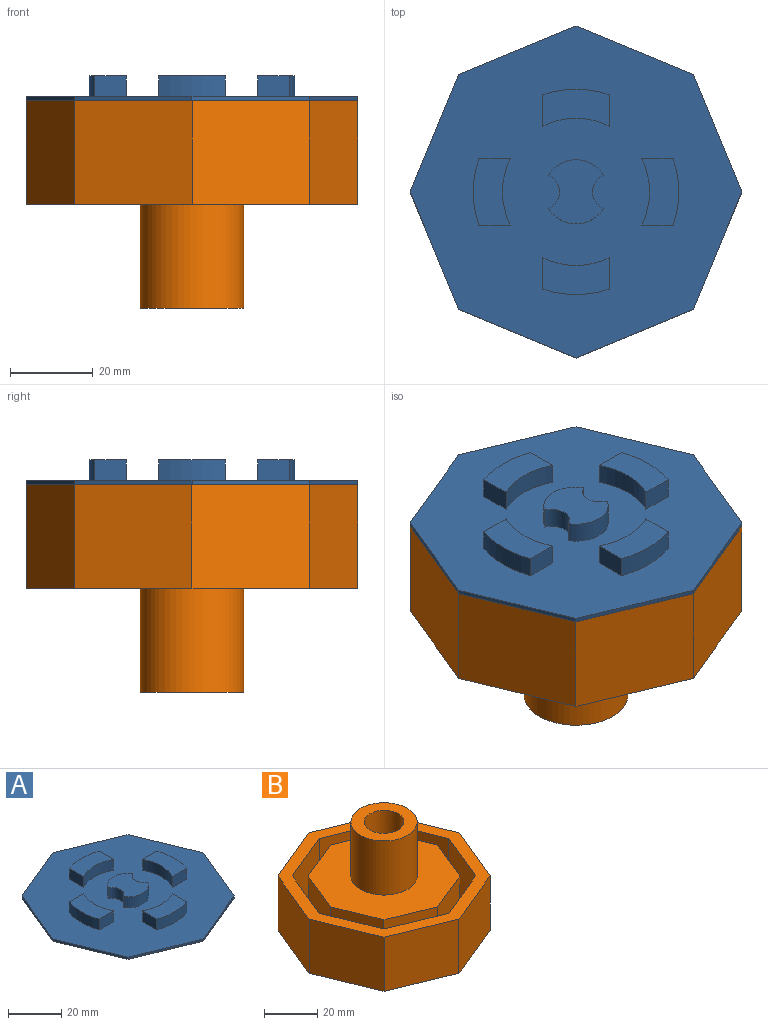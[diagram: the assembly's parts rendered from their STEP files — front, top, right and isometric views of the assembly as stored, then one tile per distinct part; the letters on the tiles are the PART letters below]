
ASSEMBLY  parts=2 mates=1
PART A: 35 faces, bbox 80x80x6 mm
  f0: plane 80x80mm, normal (0,0,1), area 3919.6mm2, adj f1,f2,f3,f4,f5,f6,f7,f8
  f1: plane 28.28x11.72mm, normal (-0.38,-0.92,0), area 30.6mm2, adj f0,f2,f8,f9
  f2: plane 28.28x11.72mm, normal (0.38,-0.92,0), area 30.6mm2, adj f0,f1,f3,f9
  f3: plane 28.28x11.72mm, normal (0.92,-0.38,0), area 30.6mm2, adj f0,f2,f4,f9
  f4: plane 28.28x11.72mm, normal (0.92,0.38,0), area 30.6mm2, adj f0,f3,f5,f9
  f5: plane 28.28x11.72mm, normal (0.38,0.92,0), area 30.6mm2, adj f0,f4,f6,f9
  f6: plane 28.28x11.72mm, normal (-0.38,0.92,0), area 30.6mm2, adj f0,f5,f7,f9
  f7: plane 28.28x11.72mm, normal (-0.92,0.38,0), area 30.6mm2, adj f0,f6,f8,f9
  f8: plane 28.28x11.72mm, normal (-0.92,-0.38,0), area 30.6mm2, adj f0,f1,f7,f9
  f9: plane 80x80mm, normal (0,0,-1), area 4525.5mm2, adj f1,f2,f3,f4,f5,f6,f7,f8
  f10: plane 7.58x5mm, normal (1,0,0), area 37.9mm2, adj f0,f11,f13,f14
  f11: cylinder r=24.75mm len=16mm, axis (0,0,-1), area 81.5mm2, adj f0,f10,f12,f14
  f12: plane 7.58x5mm, normal (-1,0,0), area 37.9mm2, adj f0,f11,f13,f14
  f13: cylinder r=17.75mm len=16mm, axis (0,0,-1), area 83mm2, adj f0,f10,f12,f14
  f14: plane 16x8.91mm, normal (0,0,1), area 114.9mm2, adj f10,f11,f12,f13
  f15: plane 16x8.91mm, normal (0,0,1), area 114.9mm2, adj f16,f17,f18,f19
  f16: cylinder r=17.75mm len=16mm, axis (0,0,-1), area 83mm2, adj f0,f15,f17,f19
  f17: plane 7.58x5mm, normal (1,0,0), area 37.9mm2, adj f0,f15,f16,f18
  f18: cylinder r=24.75mm len=16mm, axis (0,0,-1), area 81.5mm2, adj f0,f15,f17,f19
  f19: plane 7.58x5mm, normal (-1,0,0), area 37.9mm2, adj f0,f15,f16,f18
  f20: plane 16x8.91mm, normal (0,0,1), area 114.9mm2, adj f21,f22,f23,f24
  f21: plane 7.58x5mm, normal (0,-1,0), area 37.9mm2, adj f0,f20,f22,f24
  f22: cylinder r=24.75mm len=16mm, axis (0,0,-1), area 81.5mm2, adj f0,f20,f21,f23
  f23: plane 7.58x5mm, normal (0,1,0), area 37.9mm2, adj f0,f20,f22,f24
  f24: cylinder r=17.75mm len=16mm, axis (0,0,-1), area 83mm2, adj f0,f20,f21,f23
  f25: plane 7.58x5mm, normal (0,1,0), area 37.9mm2, adj f0,f26,f28,f29
  f26: cylinder r=24.75mm len=16mm, axis (0,0,-1), area 81.5mm2, adj f0,f25,f27,f29
  f27: plane 7.58x5mm, normal (0,-1,0), area 37.9mm2, adj f0,f26,f28,f29
  f28: cylinder r=17.75mm len=16mm, axis (0,0,-1), area 83mm2, adj f0,f25,f27,f29
  f29: plane 16x8.91mm, normal (0,0,1), area 114.9mm2, adj f25,f26,f27,f28
  f30: cylinder r=4.35mm len=8mm, axis (0,0,-1), area 50.7mm2, adj f0,f31,f33,f34
  f31: cylinder r=7.75mm len=13.28mm, axis (0,0,-1), area 79.7mm2, adj f0,f30,f32,f34
  f32: cylinder r=4.35mm len=8mm, axis (0,0,-1), area 50.7mm2, adj f0,f31,f33,f34
  f33: cylinder r=7.75mm len=13.28mm, axis (0,0,-1), area 79.7mm2, adj f0,f30,f32,f34
  f34: plane 15.5x13.28mm, normal (0,0,1), area 146.2mm2, adj f30,f31,f32,f33
PART B: 47 faces, bbox 80x80x50 mm
  f0: plane 20.21x20mm, normal (0.92,-0.38,0), area 400.7mm2, adj f4,f16,f35,f36,f45,f46
  f1: cylinder r=7.5mm len=41.97mm, axis (0,0,1), area 1862.2mm2, adj f2,f3,f5,f7,f9,f11,f13,f15
  f2: plane 19.24x10.11mm, normal (-0.33,0.8,-0.5), area 170.4mm2, adj f1,f15,f16,f35,f45
  f3: plane 19.1x11.5mm, normal (-0.8,-0.33,-0.5), area 170.4mm2, adj f1,f4,f35,f44,f46
  f4: plane 20.21x20mm, normal (0.38,-0.92,0), area 400.7mm2, adj f0,f3,f6,f35,f36,f44
  f5: plane 19.24x10.11mm, normal (-0.8,0.33,-0.5), area 170.4mm2, adj f1,f6,f35,f43,f44
  f6: plane 20.21x20mm, normal (-0.38,-0.92,0), area 400.7mm2, adj f4,f5,f8,f35,f36,f43
  f7: plane 19.1x11.5mm, normal (-0.33,0.8,-0.5), area 170.4mm2, adj f1,f8,f35,f42,f43
  f8: plane 20.21x20mm, normal (-0.92,-0.38,0), area 400.7mm2, adj f6,f7,f10,f35,f36,f42
  f9: plane 19.24x10.11mm, normal (0.33,0.8,-0.5), area 170.4mm2, adj f1,f10,f35,f41,f42
  f10: plane 20.21x20mm, normal (-0.92,0.38,0), area 400.7mm2, adj f8,f9,f12,f35,f36,f41
  f11: plane 19.1x11.5mm, normal (0.8,0.33,-0.5), area 170.4mm2, adj f1,f12,f35,f40,f41
  f12: plane 20.21x20mm, normal (-0.38,0.92,0), area 400.7mm2, adj f10,f11,f14,f35,f36,f40
  f13: plane 19.24x10.11mm, normal (0.8,-0.33,-0.5), area 170.4mm2, adj f1,f14,f35,f39,f40
  f14: plane 20.21x20mm, normal (0.38,0.92,0), area 400.7mm2, adj f12,f13,f16,f35,f36,f39
  f15: plane 19.1x11.5mm, normal (0.33,-0.8,-0.5), area 170.4mm2, adj f1,f2,f16,f35,f39
  f16: plane 20.21x20mm, normal (0.92,0.38,0), area 400.7mm2, adj f0,f2,f14,f15,f35,f36
  f17: plane 80x80mm, normal (0,0,1), area 1141.7mm2, adj f18,f19,f20,f21,f22,f23,f24,f25
  f18: plane 28.28x25mm, normal (0.38,0.92,0), area 765.4mm2, adj f17,f19,f25,f26
  f19: plane 28.28x25mm, normal (-0.38,0.92,0), area 765.4mm2, adj f17,f18,f20,f26
  f20: plane 28.28x25mm, normal (-0.92,0.38,0), area 765.4mm2, adj f17,f19,f21,f26
  f21: plane 28.28x25mm, normal (-0.92,-0.38,0), area 765.4mm2, adj f17,f20,f22,f26
  f22: plane 28.28x25mm, normal (-0.38,-0.92,0), area 765.4mm2, adj f17,f21,f23,f26
  f23: plane 28.28x25mm, normal (0.38,-0.92,0), area 765.4mm2, adj f17,f22,f24,f26
  f24: plane 28.28x25mm, normal (0.92,-0.38,0), area 765.4mm2, adj f17,f23,f25,f26
  f25: plane 28.28x25mm, normal (0.92,0.38,0), area 765.4mm2, adj f17,f18,f24,f26
  f26: plane 80x80mm, normal (0,0,-1), area 4525.5mm2, adj f18,f19,f20,f21,f22,f23,f24,f25
  f27: plane 24.46x20mm, normal (-0.38,-0.92,0), area 529.5mm2, adj f17,f28,f34,f35
  f28: plane 24.46x20mm, normal (0.38,-0.92,0), area 529.5mm2, adj f17,f27,f29,f35
  f29: plane 24.46x20mm, normal (0.92,-0.38,0), area 529.5mm2, adj f17,f28,f30,f35
  f30: plane 24.46x20mm, normal (0.92,0.38,0), area 529.5mm2, adj f17,f29,f31,f35
  f31: plane 24.46x20mm, normal (0.38,0.92,0), area 529.5mm2, adj f17,f30,f32,f35
  f32: plane 24.46x20mm, normal (-0.38,0.92,0), area 529.5mm2, adj f17,f31,f33,f35
  f33: plane 24.46x20mm, normal (-0.92,0.38,0), area 529.5mm2, adj f17,f32,f34,f35
  f34: plane 24.46x20mm, normal (-0.92,-0.38,0), area 529.5mm2, adj f17,f27,f33,f35
  f35: plane 69.18x69.18mm, normal (0,0,1), area 2612mm2, adj f0,f2,f3,f4,f5,f6,f7,f8
  f36: plane 57.18x57.18mm, normal (0,0,1), area 1820.7mm2, adj f0,f4,f6,f8,f10,f12,f14,f16
  f37: cylinder r=12.5mm len=25mm, axis (0,0,-1), area 1963.5mm2, adj f36,f38
  f38: plane 25x25mm, normal (0,0,1), area 314.2mm2, adj f1,f37
  f39: plane 19.1x11.5mm, normal (-0.8,0.33,-0.5), area 170.4mm2, adj f1,f13,f14,f15,f35
  f40: plane 19.24x10.11mm, normal (-0.8,-0.33,-0.5), area 170.4mm2, adj f1,f11,f12,f13,f35
  f41: plane 19.1x11.5mm, normal (-0.33,-0.8,-0.5), area 170.4mm2, adj f1,f9,f10,f11,f35
  f42: plane 19.24x10.11mm, normal (0.33,-0.8,-0.5), area 170.4mm2, adj f1,f7,f8,f9,f35
  f43: plane 19.1x11.5mm, normal (0.8,-0.33,-0.5), area 170.4mm2, adj f1,f5,f6,f7,f35
  f44: plane 19.24x10.11mm, normal (0.8,0.33,-0.5), area 170.4mm2, adj f1,f3,f4,f5,f35
  f45: plane 19.24x10.11mm, normal (-0.33,-0.8,-0.5), area 170.4mm2, adj f0,f1,f2,f35,f46
  f46: plane 19.1x11.5mm, normal (0.33,0.8,-0.5), area 170.4mm2, adj f0,f1,f3,f35,f45
PLACE A t=(-10.39,11.38,19.77)mm
PLACE B rot(axis=(1,0,0),180deg) t=(-10.39,11.38,18.77)mm
MATE fastened B.f1 <-> A.f33  axis (0,0,1) through (-10.39,11.38,18.77)mm
